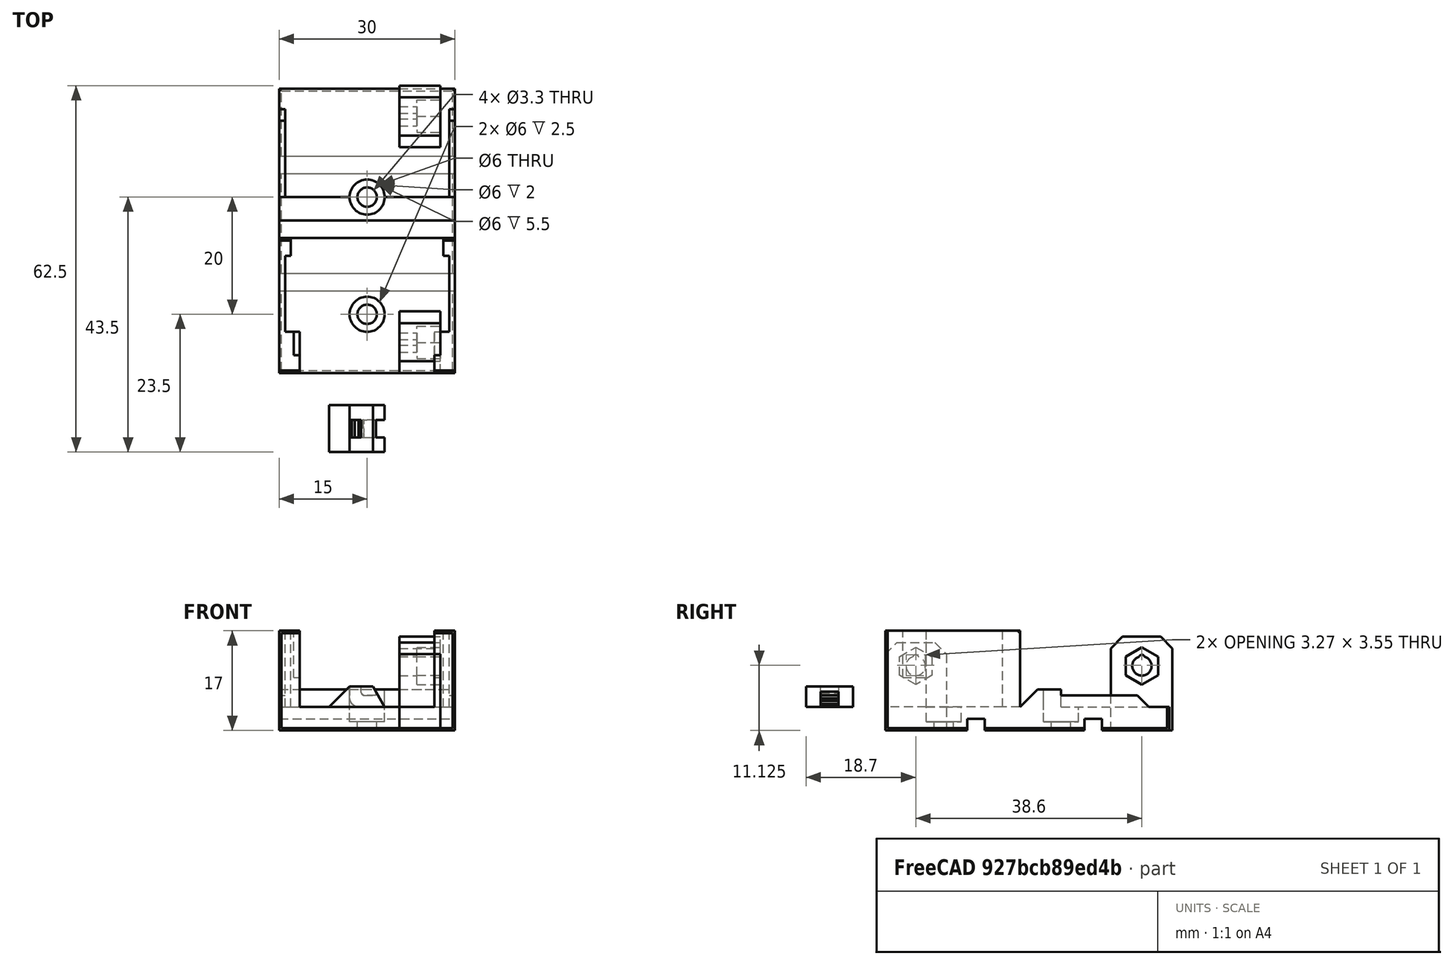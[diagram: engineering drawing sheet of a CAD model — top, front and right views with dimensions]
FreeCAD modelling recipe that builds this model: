
FCSTD DOCUMENT  (FreeCAD 0.18R14555 (Git shallow))
Label: bear-power-connector-mounter-4-pins
License: All rights reserved
LicenseURL: http://en.wikipedia.org/wiki/All_rights_reserved
objects: Part::Box×16, Part::Cut×10, Part::Cylinder×8, Part::MultiFuse×8, Part::Feature×6, Part::Chamfer×6
note: 54 computed .brp shape members not serialized (recipe doc carries the construction recipe); baked Part::Feature solids carry a one-line shape summary decoded from their .brp

FEATURE [Part::Box] Box  label="Cube"
  AttacherType = Attacher::AttachEngine3D
  Height = 4
  Length = 30
  Placement = pos=(0,-24.5,0) rot=(0,0,1;0rad)
  Width = 48.5
FEATURE [Part::Box] Box001  label="Cube001"
  AttacherType = Attacher::AttachEngine3D
  Height = 16
  Length = 7
  Placement = pos=(20.5,14,0) rot=(0,0,1;0rad)
  Width = 10.5
FEATURE [Part::Feature] Body001
  Placement = pos=(23.5,19.3,11) rot=(0,0,1;0rad)
  shape: bbox 10 x 5.543 x 6.4 mm, 8 faces (baked)
FEATURE [Part::Feature] Body002
  Placement = pos=(23.5,-19.3,11) rot=(0,0,1;0rad)
  shape: bbox 10 x 5.543 x 6.4 mm, 8 faces (baked)
FEATURE [Part::Box] Box002  label="Cube002"
  AttacherType = Attacher::AttachEngine3D
  Height = 15
  Length = 7
  Placement = pos=(20.5,-24.5,0) rot=(0,0,1;0rad)
  Width = 10.5
FEATURE [Part::Cylinder] Cylinder
  Angle = 360
  AttacherType = Attacher::AttachEngine3D
  Height = 10
  Placement = pos=(20.5,19.3,12.4) rot=(0,1,0;1.5708rad)
  Radius = 0.5
FEATURE [Part::Cylinder] Cylinder001
  Angle = 360
  AttacherType = Attacher::AttachEngine3D
  Height = 10
  Placement = pos=(20.5,-19.3,12.4) rot=(0,1,0;1.5708rad)
  Radius = 0.5
FEATURE [Part::Cylinder] Cylinder002
  Angle = 360
  AttacherType = Attacher::AttachEngine3D
  Height = 10
  Placement = pos=(20.5,19.3,11) rot=(0,1,0;1.5708rad)
  Radius = 1.65
FEATURE [Part::Cylinder] Cylinder003
  Angle = 360
  AttacherType = Attacher::AttachEngine3D
  Height = 10
  Placement = pos=(20.5,-19.3,11) rot=(0,1,0;1.5708rad)
  Radius = 1.65
FEATURE [Part::Cut] Cut
  Base = -> Box001
  Tool = -> Cylinder002
FEATURE [Part::Cut] Cut001
  Base = -> Box002
  Tool = -> Cylinder003
FEATURE [Part::Cut] Cut002
  Base = -> Cut
  Tool = -> Cylinder
FEATURE [Part::Cut] Cut003
  Base = -> Cut001
  Tool = -> Cylinder001
FEATURE [Part::Cut] Cut004
  Base = -> Cut002
  Tool = -> Body001
FEATURE [Part::Cut] Cut005
  Base = -> Cut003
  Tool = -> Body002
FEATURE [Part::Chamfer] Chamfer
  Base = -> Cut005
  Edges = 2 edges r=2: [Edge10,Edge11]
FEATURE [Part::Chamfer] Chamfer001
  Base = -> Cut004
  Edges = 2 edges r=2: [Edge10,Edge11]
FEATURE [Part::Box] Box003  label="Cube003"
  AttacherType = Attacher::AttachEngine3D
  Height = 17
  Length = 3.5
  Placement = pos=(0,-24.5,0) rot=(0,0,1;0rad)
  Width = 7
FEATURE [Part::Box] Box004  label="Cube004"
  AttacherType = Attacher::AttachEngine3D
  Height = 17
  Length = 3.5
  Placement = pos=(26.5,-24.5,0) rot=(0,0,1;0rad)
  Width = 7
FEATURE [Part::Box] Box005  label="Cube005"
  AttacherType = Attacher::AttachEngine3D
  Height = 17
  Length = 1
  Placement = pos=(0,-17.5,0) rot=(0,0,1;0rad)
  Width = 13
FEATURE [Part::Box] Box006  label="Cube006"
  AttacherType = Attacher::AttachEngine3D
  Height = 17
  Length = 1
  Placement = pos=(29,-17.5,0) rot=(0,0,1;0rad)
  Width = 13
FEATURE [Part::Box] Box007  label="Cube007"
  AttacherType = Attacher::AttachEngine3D
  Height = 17
  Length = 2
  Placement = pos=(0,-4.5,0) rot=(0,0,1;0rad)
  Width = 3
FEATURE [Part::Box] Box008  label="Cube008"
  AttacherType = Attacher::AttachEngine3D
  Height = 17
  Length = 2
  Placement = pos=(28,-4.5,0) rot=(0,0,1;0rad)
  Width = 3
FEATURE [Part::Box] Box009  label="Cube009"
  AttacherType = Attacher::AttachEngine3D
  Height = 8
  Length = 1
  Placement = pos=(2.5,-21.5,9) rot=(0,0,1;0rad)
  Width = 4
FEATURE [Part::Box] Box010  label="Cube010"
  AttacherType = Attacher::AttachEngine3D
  Height = 8
  Length = 1
  Placement = pos=(26.5,-21.5,9) rot=(0,0,1;0rad)
  Width = 4
FEATURE [Part::Cut] Cut006
  Base = -> Box004
  Tool = -> Box010
FEATURE [Part::Cut] Cut007
  Base = -> Box003
  Tool = -> Box009
FEATURE [Part::MultiFuse] Fusion
  Shapes = -> [Cut007,Box005,Box007]
FEATURE [Part::MultiFuse] Fusion001
  Shapes = -> [Cut006,Box006,Box008]
FEATURE [Part::Feature] Part__Feature  label="Common002"
  Placement = pos=(-12,-15.5,66.75) rot=(0.57735,-0.57735,0.57735;4.18879rad)
  shape: bbox 9.5 x 8 x 3.5 mm, 30 faces (baked)
FEATURE [Part::Box] Box011  label="Cube011"
  AttacherType = Attacher::AttachEngine3D
  Height = 2
  Length = 36
  Placement = pos=(-3,-10.5,0) rot=(0,0,1;0rad)
  Width = 3
FEATURE [Part::Box] Box012  label="Cube012"
  AttacherType = Attacher::AttachEngine3D
  Height = 2
  Length = 36
  Placement = pos=(-3,9.5,0) rot=(0,0,1;0rad)
  Width = 3
FEATURE [Part::Cylinder] Cylinder004
  Angle = 360
  AttacherType = Attacher::AttachEngine3D
  Height = 2.5
  Placement = pos=(15,17,1.5) rot=(0,0,1;0rad)
  Radius = 3
FEATURE [Part::Cylinder] Cylinder005
  Angle = 360
  AttacherType = Attacher::AttachEngine3D
  Height = 2.5
  Placement = pos=(15,-17,1.5) rot=(0,0,1;0rad)
  Radius = 3
FEATURE [Part::Cylinder] Cylinder006
  Angle = 360
  AttacherType = Attacher::AttachEngine3D
  Height = 10
  Placement = pos=(15,-17,0) rot=(0,0,1;0rad)
  Radius = 1.65
FEATURE [Part::Cylinder] Cylinder007
  Angle = 360
  AttacherType = Attacher::AttachEngine3D
  Height = 10
  Placement = pos=(15,17,0) rot=(0,0,1;0rad)
  Radius = 1.65
FEATURE [Part::Box] Box013  label="Cube013"
  AttacherType = Attacher::AttachEngine3D
  Height = 7
  Length = 30
  Placement = pos=(0,-1.5,0) rot=(0,0,1;0rad)
  Width = 7
FEATURE [Part::Chamfer] Chamfer002
  Base = -> Box013
  Edges = 1 edges r=3: [Edge10]
FEATURE [Part::Box] Box014  label="Cube014"
  AttacherType = Attacher::AttachEngine3D
  Height = 6
  Length = 1
  Placement = pos=(0,5.5,0) rot=(0,0,1;0rad)
  Width = 15
FEATURE [Part::Box] Box015  label="Cube015"
  AttacherType = Attacher::AttachEngine3D
  Height = 6
  Length = 1
  Placement = pos=(29,5.5,0) rot=(0,0,1;0rad)
  Width = 15
FEATURE [Part::MultiFuse] Fusion003
  Shapes = -> [Box011,Box012]
FEATURE [Part::Chamfer] Chamfer003
  Base = -> Box015
  Edges = 1 edges r=2: [Edge12]
FEATURE [Part::Chamfer] Chamfer004
  Base = -> Box014
  Edges = 1 edges r=2: [Edge12]
FEATURE [Part::MultiFuse] Fusion004
  Placement = pos=(0,2.5,0) rot=(0,0,1;0rad)
  Shapes = -> [Cylinder006,Cylinder005]
FEATURE [Part::MultiFuse] Fusion005
  Placement = pos=(0,-11.5,0) rot=(0,0,1;0rad)
  Shapes = -> [Cylinder007,Cylinder004]
FEATURE [Part::Feature] Fusion005001  label="Fusion006"
  Placement = pos=(0,-11.5,2) rot=(0,0,1;0rad)
  shape: bbox 6 x 6 x 10 mm, 7 faces (baked)
FEATURE [Part::Feature] Fusion005002  label="Fusion007"
  Placement = pos=(0,-11.5,3) rot=(0,0,1;0rad)
  shape: bbox 6 x 6 x 10 mm, 7 faces (baked)
FEATURE [Part::MultiFuse] Fusion005003
  Shapes = -> [Fusion005002,Fusion005001,Fusion005]
FEATURE [Part::MultiFuse] Fusion005005
  Shapes = -> [Fusion004,Fusion005003]
FEATURE [Part::MultiFuse] Fusion005006
  Shapes = -> [Fusion001,Fusion,Chamfer003,Chamfer002,Box,Chamfer004]
FEATURE [Part::Cut] Cut008
  Base = -> Fusion005006
  Tool = -> Fusion005005
FEATURE [Part::Cut] Cut009
  Base = -> Cut008
  Tool = -> Fusion003
FEATURE [Part::Feature] Cut009001  label="Cut010"
  shape: bbox 30 x 48.5 x 17 mm, 51 faces (baked)
FEATURE [Part::Chamfer] Chamfer005
  Base = -> Cut009001
  Edges = 16 edges r=0.4: [Edge11,Edge12,Edge21,Edge22,Edge26,Edge29,Edge94,Edge110,Edge111,Edge129,Edge135,Edge136,Edge137,Edge138,Edge139,Edge140]
